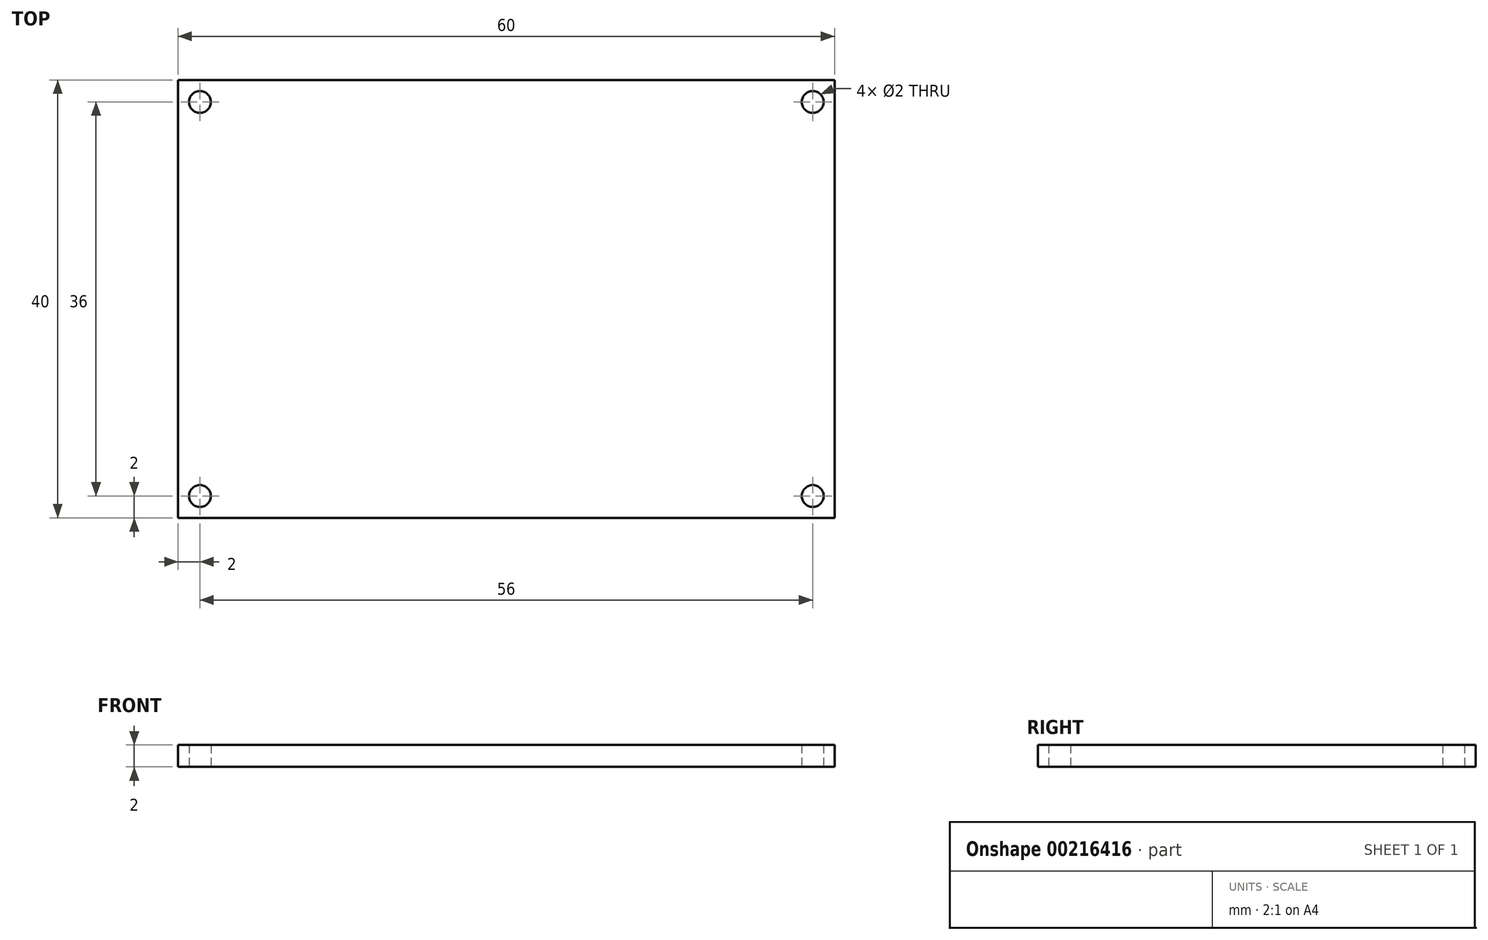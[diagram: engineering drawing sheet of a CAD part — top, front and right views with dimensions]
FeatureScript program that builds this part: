
annotation { "Feature Type Name" : "Feature", "Feature Type Description" : "" }
export const myFeature = defineFeature(function(context is Context, id is Id, definition is map)
    precondition{}
    {
        {
            var Q0;
            Q0=qCreatedBy(makeId("Top.planeOp"),FACE);
            var sketch = newSketch(context, id + "F0", { "sketchPlane" : qUnion([Q0])});
            skLineSegment(sketch, "E0.bottom", {"start": v(-30, 20) * mm, "end": v(30, 20) * mm});
            skLineSegment(sketch, "E0.top", {"start": v(-30, -20) * mm, "end": v(30, -20) * mm});
            skLineSegment(sketch, "E0.left", {"start": v(-30, 20) * mm, "end": v(-30, -20) * mm});
            skLineSegment(sketch, "E0.right", {"start": v(30, 20) * mm, "end": v(30, -20) * mm});
            skCircle(sketch, "E1", {"center": v(-28, 18) * mm, "radius": 1 * mm});
            skCircle(sketch, "E2.MirrorC", {"center": v(28, 18) * mm, "radius": 1 * mm});
            skCircle(sketch, "E3.MirrorC", {"center": v(-28, -18) * mm, "radius": 1 * mm});
            skCircle(sketch, "E4.MirrorC", {"center": v(28, -18) * mm, "radius": 1 * mm});
            skSolve(sketch);
        }
        {
            var Q0;
            Q0=makeQuery(id+"F0.imprint","IMPRINT",FACE,{"disambiguationData":[TD([[makeQuery(id+"F0.imprint","IMPRINT",EDGE,{"derivedFrom":sQuery(id+"F0.wireOp",EDGE,"E0.bottom")}),-1.0]])]});
            extrude(context, id + "F1", {"entities" : qUnion([Q0]), "depth" : 2 * mm});
        }
    });
